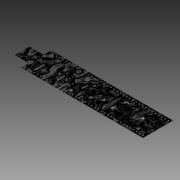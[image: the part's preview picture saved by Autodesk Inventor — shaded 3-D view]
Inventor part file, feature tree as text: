
AUTODESK INVENTOR PART (.ipt)
format: ipt  version: 2018 (Build 220112000, 112)  size: 2,497,024 bytes
history: native  units: mm
features: extrude x5, pattern_linear x3, mirror x3, plane x2, fillet x2, sketch x1, other x1
ambient origin geometry x8: Origin, YZ Plane, XZ Plane, XY Plane, X Axis, Y Axis, Z Axis, Center Point
bodies: Solid1 (feature_tree)
feature tree (17):
  sketch  "Sketch1"  dims[d0=11.99mm d1=11.35mm d2=24.13mm d3=97.54mm d23=70.0mm d25=2.57mm d26=10.0mm d28=10.0mm d31=1.0mm d32=260.0mm d34=2.56mm d35=10.0mm d37=10.0mm d40=1.0mm d41=50.0mm d43=2.55mm d44=10.0mm d46=10.0mm d49=0.0787mm d50=0.0mm d52=0.0787mm d53=0.0mm d54=70.0mm d56=2.55mm d57=0.0787mm d58=0.0mm d59=260.0mm d61=2.56mm d62=0.0787mm d63=0.0mm d64=50.0mm d66=2.55mm d67=6.5mm d68=0.0787mm d69=0.0mm d70=0.05mm d71=0.05mm]
  extrude  "Extrusion1"  Depth=11.35mm
  extrude  "Extrusion2"  Depth=24.13mm
  pattern_linear  "Rectangular Pattern1"  Spacing1=97.54mm  [1 undecoded]
  extrude  "Extrusion3"  Depth=10.0mm
  pattern_linear  "Rectangular Pattern2"  Spacing1=1.0mm  [1 undecoded]
  plane  "Work Plane1"
  mirror  "Mirror1"
  extrude  "Extrusion4"  Depth=10.0mm
  pattern_linear  "Rectangular Pattern3"  Spacing1=1.0mm  [1 undecoded]
  extrude  "Extrusion5"  Depth=10.0mm
  fillet  "Fillet1"  Radius=0.0787mm
  mirror  "Mirror2"
  plane  "Work Plane2"
  mirror  "Mirror3"
  fillet  "Fillet2"  Radius=0.0787mm
  other  "Image1"
note: 3 required parameter values undecoded (feature->parameter linkage not recoverable at this tier; creation-order binding heuristic only, values carry confidence <= 0.55)
